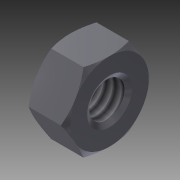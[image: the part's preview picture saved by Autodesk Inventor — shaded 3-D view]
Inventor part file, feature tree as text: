
AUTODESK INVENTOR PART (.ipt)
format: ipt  version: 2018 (Build 220112000, 112)  size: 171,008 bytes
history: native  units: mm (DEFAULTED — no unit token found)
features: sketch x3, chamfer x1, hole x1
ambient origin geometry x8: Origin, YZ Plane, XZ Plane, XY Plane, X Axis, Y Axis, Z Axis, Center Point
bodies: Solid1 (feature_tree), Body (feature_tree)
feature tree (5):
  chamfer  "Chamfer1"  Angle=30.0deg  [1 undecoded]
  hole  "Thread"  [1 undecoded]
  sketch  "Sketch1"  dims[d0=12.83161mm]
  sketch  "Sketch2"  dims[d1=5.5626mm]
  sketch  "Sketch3"  dims[d2=0.0mm d3=30.0deg d4=30.0deg d5=11.1125mm d6=11.1125mm d7=90.0deg d25=4.9784mm d26=6.0mm d27=4.0mm d28=2.0mm d29=14.3117mm d30=8.0mm d31=20.594885mm d8=0.687408mm d9=30.0deg d10=0.687408mm d11=30.0deg d13=0.0mm d14=0.0mm d39=0.0mm d40=0.687408mm d41=0.687408mm]
note: 2 required parameter values undecoded (feature->parameter linkage not recoverable at this tier; creation-order binding heuristic only, values carry confidence <= 0.55)
